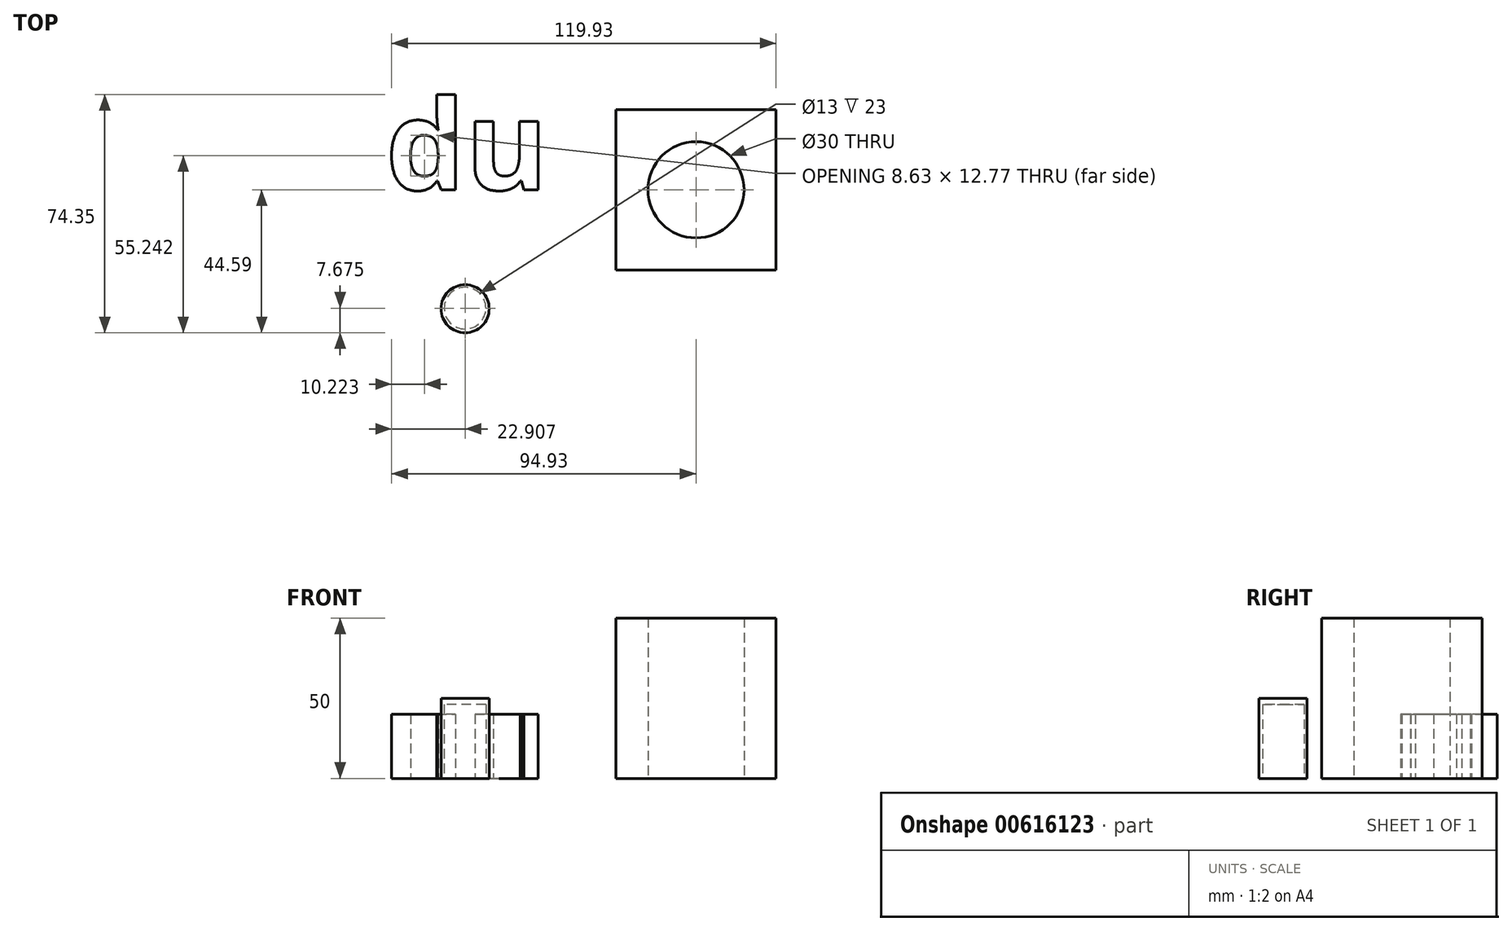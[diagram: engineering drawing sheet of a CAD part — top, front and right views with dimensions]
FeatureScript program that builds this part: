
annotation { "Feature Type Name" : "Feature", "Feature Type Description" : "" }
export const myFeature = defineFeature(function(context is Context, id is Id, definition is map)
    precondition{}
    {
        {
            var Q0;
            Q0=qCreatedBy(makeId("Top.planeOp"),FACE);
            var sketch = newSketch(context, id + "F0", { "sketchPlane" : qUnion([Q0])});
            skLineSegment(sketch, "E0.bottom", {"start": v(25, -25) * mm, "end": v(-25, -25) * mm});
            skLineSegment(sketch, "E0.top", {"start": v(25, 25) * mm, "end": v(-25, 25) * mm});
            skLineSegment(sketch, "E0.left", {"start": v(25, -25) * mm, "end": v(25, 25) * mm});
            skLineSegment(sketch, "E0.right", {"start": v(-25, -25) * mm, "end": v(-25, 25) * mm});
            skPoint(sketch, "E0.middle", {"position": v(0, 0) * mm});
            skCircle(sketch, "E1", {"center": v(0, 0) * mm, "radius": 15 * mm});
            skSolve(sketch);
        }
        {
            var Q0;
            Q0=makeQuery(id+"F0.imprint","IMPRINT",FACE,{"disambiguationData":[TD([[makeQuery(id+"F0.imprint","IMPRINT",EDGE,{"derivedFrom":sQuery(id+"F0.wireOp",EDGE,"E0.bottom")}),-1.0]])]});
            extrude(context, id + "F1", {"entities" : qUnion([Q0]), "depth" : 50 * mm, "offsetDistance" : 25 * mm});
        }
        {
            var Q0;
            Q0=qCreatedBy(makeId("Top.planeOp"),FACE);
            var sketch = newSketch(context, id + "F2", { "sketchPlane" : qUnion([Q0])});
            skText(sketch, "E2", { "text": "du   ", "fontName": "OpenSans-Bold.ttf"});
            const initialGuessF2  = {"E2": [-0.09669, 0, 1, 0, 0.0282]};
            skSetInitialGuess(sketch, initialGuessF2);
            skSolve(sketch);
        }
        {
            var Q0;
            Q0 = qSketchRegion(id + "F2", true);
            extrude(context, id + "F3", {"entities" : qUnion([Q0]), "depth" : 20 * mm, "offsetDistance" : 25 * mm});
        }
        {
            var Q0;
            Q0=qCreatedBy(makeId("Top.planeOp"),FACE);
            var sketch = newSketch(context, id + "F4", { "sketchPlane" : qUnion([Q0])});
            skCircle(sketch, "E3", {"center": v(-72, -37.1) * mm, "radius": 7.5 * mm});
            skSolve(sketch);
        }
        {
            var Q0;
            Q0 = qSketchRegion(id + "F4", true);
            extrude(context, id + "F5", {"entities" : qUnion([Q0]), "depth" : 25 * mm, "offsetDistance" : 25 * mm});
        }
        {
            var Q0;
            Q0=qCreatedBy(makeId("Top.planeOp"),FACE);
            var sketch = newSketch(context, id + "F6", { "sketchPlane" : qUnion([Q0])});
            skCircle(sketch, "E4", {"center": v(-72.02, -36.91) * mm, "radius": 6.5 * mm});
            skSolve(sketch);
        }
        {
            var Q0;
            Q0 = qSketchRegion(id + "F6", true);
            extrude(context, id + "F7", {"entities" : qUnion([Q0]), "operationType" : NewBodyOperationType.REMOVE, "depth" : 23 * mm, "offsetDistance" : 25 * mm});
        }
    });
